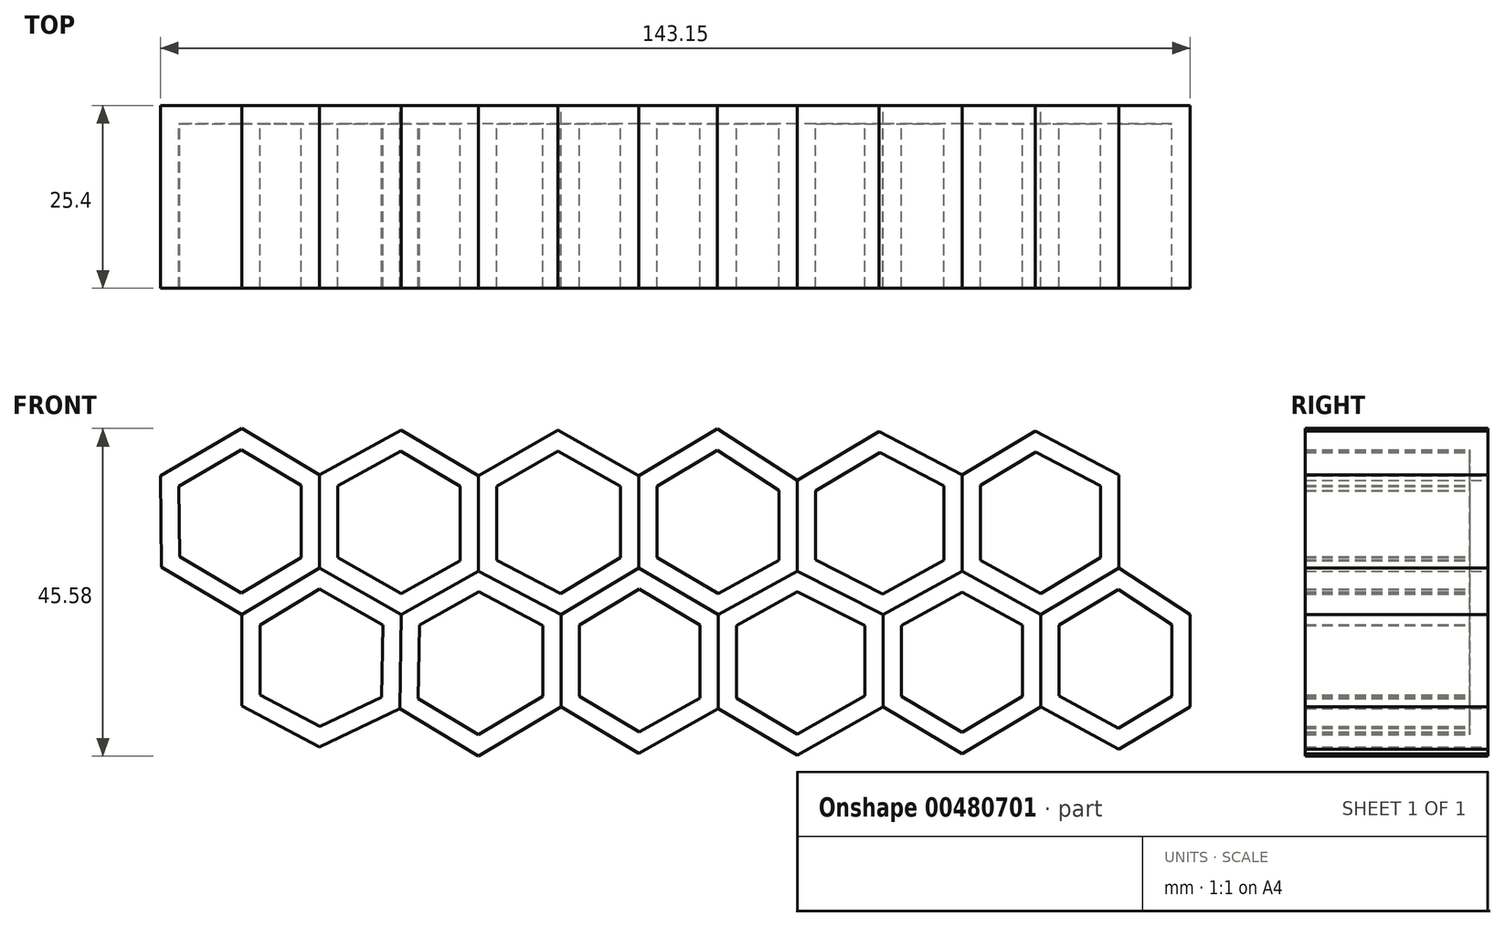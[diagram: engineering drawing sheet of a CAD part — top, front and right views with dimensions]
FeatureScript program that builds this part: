
annotation { "Feature Type Name" : "Feature", "Feature Type Description" : "" }
export const myFeature = defineFeature(function(context is Context, id is Id, definition is map)
    precondition{}
    {
        {
            var Q0;
            Q0=qCreatedBy(makeId("Front.planeOp"),FACE);
            var sketch = newSketch(context, id + "F0", { "sketchPlane" : qUnion([Q0])});
            skLineSegment(sketch, "E0", {"start": v(-72.86, 44.97) * mm, "end": v(-61.6, 51.55) * mm});
            skLineSegment(sketch, "E1", {"start": v(-61.6, 51.55) * mm, "end": v(-50.77, 45.08) * mm});
            skLineSegment(sketch, "E2", {"start": v(-50.77, 45.08) * mm, "end": v(-50.77, 32.14) * mm});
            skLineSegment(sketch, "E3", {"start": v(-50.77, 32.14) * mm, "end": v(-61.6, 25.66) * mm});
            skLineSegment(sketch, "E4", {"start": v(-61.6, 25.66) * mm, "end": v(-72.75, 32.25) * mm});
            skLineSegment(sketch, "E5", {"start": v(-72.75, 32.25) * mm, "end": v(-72.86, 44.97) * mm});
            skLineSegment(sketch, "E6", {"start": v(-50.77, 45.08) * mm, "end": v(-39.39, 51.33) * mm});
            skLineSegment(sketch, "E7", {"start": v(-39.39, 51.33) * mm, "end": v(-28.68, 44.97) * mm});
            skLineSegment(sketch, "E8", {"start": v(-28.68, 44.97) * mm, "end": v(-28.68, 31.69) * mm});
            skLineSegment(sketch, "E9", {"start": v(-28.68, 31.69) * mm, "end": v(-39.39, 25.66) * mm});
            skLineSegment(sketch, "E10", {"start": v(-39.39, 25.66) * mm, "end": v(-50.77, 32.14) * mm});
            skLineSegment(sketch, "E11", {"start": v(-28.68, 44.97) * mm, "end": v(-17.63, 51.33) * mm});
            skLineSegment(sketch, "E12", {"start": v(-17.63, 51.33) * mm, "end": v(-6.36, 44.97) * mm});
            skLineSegment(sketch, "E13", {"start": v(-6.36, 44.97) * mm, "end": v(-6.36, 32.14) * mm});
            skLineSegment(sketch, "E14", {"start": v(-6.36, 32.14) * mm, "end": v(-17.18, 25.66) * mm});
            skLineSegment(sketch, "E15", {"start": v(-17.18, 25.66) * mm, "end": v(-28.68, 31.69) * mm});
            skLineSegment(sketch, "E16", {"start": v(-6.36, 44.97) * mm, "end": v(4.57, 51.5) * mm});
            skLineSegment(sketch, "E17", {"start": v(4.57, 51.5) * mm, "end": v(15.63, 44.3) * mm});
            skLineSegment(sketch, "E18", {"start": v(15.63, 44.3) * mm, "end": v(15.63, 31.69) * mm});
            skLineSegment(sketch, "E19", {"start": v(15.63, 31.69) * mm, "end": v(4.65, 25.66) * mm});
            skLineSegment(sketch, "E20", {"start": v(4.65, 25.66) * mm, "end": v(-6.36, 32.14) * mm});
            skLineSegment(sketch, "E21", {"start": v(15.63, 44.3) * mm, "end": v(27.04, 51.13) * mm});
            skLineSegment(sketch, "E22", {"start": v(27.04, 51.13) * mm, "end": v(38.57, 45.08) * mm});
            skLineSegment(sketch, "E23", {"start": v(38.57, 45.08) * mm, "end": v(38.57, 31.69) * mm});
            skLineSegment(sketch, "E24", {"start": v(38.57, 31.69) * mm, "end": v(27.6, 25.66) * mm});
            skLineSegment(sketch, "E25", {"start": v(27.6, 25.66) * mm, "end": v(15.63, 31.69) * mm});
            skLineSegment(sketch, "E26", {"start": v(38.57, 45.08) * mm, "end": v(48.75, 51.16) * mm});
            skLineSegment(sketch, "E27", {"start": v(48.75, 51.16) * mm, "end": v(60.35, 45.08) * mm});
            skLineSegment(sketch, "E28", {"start": v(60.35, 45.08) * mm, "end": v(60.35, 32.14) * mm});
            skLineSegment(sketch, "E29", {"start": v(60.35, 32.14) * mm, "end": v(49.52, 25.66) * mm});
            skLineSegment(sketch, "E30", {"start": v(49.52, 25.66) * mm, "end": v(38.57, 31.69) * mm});
            skLineSegment(sketch, "E31", {"start": v(-61.6, 25.66) * mm, "end": v(-61.6, 12.94) * mm});
            skLineSegment(sketch, "E32", {"start": v(-61.6, 12.94) * mm, "end": v(-50.77, 7.26) * mm});
            skLineSegment(sketch, "E33", {"start": v(-50.77, 7.26) * mm, "end": v(-39.6, 12.56) * mm});
            skLineSegment(sketch, "E34", {"start": v(-39.6, 12.56) * mm, "end": v(-39.39, 25.66) * mm});
            skLineSegment(sketch, "E35", {"start": v(-17.18, 25.66) * mm, "end": v(-17.18, 12.84) * mm});
            skLineSegment(sketch, "E36", {"start": v(-17.18, 12.84) * mm, "end": v(-28.68, 5.97) * mm});
            skLineSegment(sketch, "E37", {"start": v(-28.68, 5.97) * mm, "end": v(-39.6, 12.56) * mm});
            skLineSegment(sketch, "E38", {"start": v(4.65, 25.66) * mm, "end": v(4.65, 12.56) * mm});
            skLineSegment(sketch, "E39", {"start": v(4.65, 12.56) * mm, "end": v(-6.36, 6.37) * mm});
            skLineSegment(sketch, "E40", {"start": v(-6.36, 6.37) * mm, "end": v(-17.18, 12.84) * mm});
            skLineSegment(sketch, "E41", {"start": v(27.6, 25.66) * mm, "end": v(27.6, 12.84) * mm});
            skLineSegment(sketch, "E42", {"start": v(27.6, 12.84) * mm, "end": v(15.63, 6.11) * mm});
            skLineSegment(sketch, "E43", {"start": v(15.63, 6.11) * mm, "end": v(4.65, 12.56) * mm});
            skLineSegment(sketch, "E44", {"start": v(49.52, 25.66) * mm, "end": v(49.52, 12.84) * mm});
            skLineSegment(sketch, "E45", {"start": v(49.52, 12.84) * mm, "end": v(38.57, 6.3) * mm});
            skLineSegment(sketch, "E46", {"start": v(38.57, 6.3) * mm, "end": v(27.6, 12.84) * mm});
            skLineSegment(sketch, "E47", {"start": v(60.35, 32.14) * mm, "end": v(70.29, 25.66) * mm});
            skLineSegment(sketch, "E48", {"start": v(70.29, 25.66) * mm, "end": v(70.29, 12.84) * mm});
            skLineSegment(sketch, "E49", {"start": v(70.29, 12.84) * mm, "end": v(60.35, 6.9) * mm});
            skLineSegment(sketch, "E50", {"start": v(60.35, 6.9) * mm, "end": v(49.52, 12.84) * mm});
            skSolve(sketch);
        }
        {
            var Q0;
            Q0=makeQuery(id+"F0.imprint","IMPRINT",FACE,{"disambiguationData":[TD([[makeQuery(id+"F0.imprint","IMPRINT",EDGE,{"derivedFrom":sQuery(id+"F0.wireOp",EDGE,"E0")}),-1.0]])]});
            var Q1;
            Q1=makeQuery(id+"F0.imprint","IMPRINT",FACE,{"disambiguationData":[TD([[makeQuery(id+"F0.imprint","IMPRINT",EDGE,{"derivedFrom":sQuery(id+"F0.wireOp",EDGE,"E29")}),1.0]])]});
            var Q2;
            Q2=makeQuery(id+"F0.imprint","IMPRINT",FACE,{"disambiguationData":[TD([[makeQuery(id+"F0.imprint","IMPRINT",EDGE,{"derivedFrom":sQuery(id+"F0.wireOp",EDGE,"E18")}),1.0]])]});
            var Q3;
            Q3=makeQuery(id+"F0.imprint","IMPRINT",FACE,{"disambiguationData":[TD([[makeQuery(id+"F0.imprint","IMPRINT",EDGE,{"derivedFrom":sQuery(id+"F0.wireOp",EDGE,"E14")}),1.0]])]});
            extrude(context, id + "F1", {"entities" : qUnion([Q0, Q1, Q2, Q3]), "depth" : 25.4 * mm});
        }
        {
            var Q0;
            Q0=makeQuery(id+"F1.opExtrude","CAP_FACE",FACE,{"disambiguationData":[OSD([sQuery(id+"F0.wireOp",EDGE,"E0"),sQuery(id+"F0.wireOp",EDGE,"E1"),sQuery(id+"F0.wireOp",EDGE,"E2"),sQuery(id+"F0.wireOp",EDGE,"E3"),sQuery(id+"F0.wireOp",EDGE,"E4"),sQuery(id+"F0.wireOp",EDGE,"E5")])],"isStart":false});
            var Q1;
            Q1=makeQuery(id+"F1.opExtrude","CAP_FACE",FACE,{"disambiguationData":[OSD([sQuery(id+"F0.wireOp",EDGE,"E14"),sQuery(id+"F0.wireOp",EDGE,"E20"),sQuery(id+"F0.wireOp",EDGE,"E35"),sQuery(id+"F0.wireOp",EDGE,"E38"),sQuery(id+"F0.wireOp",EDGE,"E39"),sQuery(id+"F0.wireOp",EDGE,"E40")])],"isStart":false});
            var Q2;
            Q2=makeQuery(id+"F1.opExtrude","CAP_FACE",FACE,{"disambiguationData":[OSD([sQuery(id+"F0.wireOp",EDGE,"E18"),sQuery(id+"F0.wireOp",EDGE,"E21"),sQuery(id+"F0.wireOp",EDGE,"E22"),sQuery(id+"F0.wireOp",EDGE,"E23"),sQuery(id+"F0.wireOp",EDGE,"E24"),sQuery(id+"F0.wireOp",EDGE,"E25")])],"isStart":false});
            var Q3;
            Q3=makeQuery(id+"F1.opExtrude","CAP_FACE",FACE,{"disambiguationData":[OSD([sQuery(id+"F0.wireOp",EDGE,"E29"),sQuery(id+"F0.wireOp",EDGE,"E44"),sQuery(id+"F0.wireOp",EDGE,"E47"),sQuery(id+"F0.wireOp",EDGE,"E48"),sQuery(id+"F0.wireOp",EDGE,"E49"),sQuery(id+"F0.wireOp",EDGE,"E50")])],"isStart":false});
            shell(context, id + "F2", {"entities" : qUnion([Q0, Q1, Q2, Q3]), "thickness" : 2.54 * mm});
        }
        {
            var Q0;
            Q0=makeQuery(id+"F0.imprint","IMPRINT",FACE,{"disambiguationData":[TD([[makeQuery(id+"F0.imprint","IMPRINT",EDGE,{"derivedFrom":sQuery(id+"F0.wireOp",EDGE,"E2")}),1.0]])]});
            var Q1;
            Q1=makeQuery(id+"F0.imprint","IMPRINT",FACE,{"disambiguationData":[TD([[makeQuery(id+"F0.imprint","IMPRINT",EDGE,{"derivedFrom":sQuery(id+"F0.wireOp",EDGE,"E13")}),1.0]])]});
            extrude(context, id + "F3", {"entities" : qUnion([Q0, Q1]), "depth" : 25.4 * mm});
        }
        {
            var Q0;
            Q0=makeQuery(id+"F3.opExtrude","CAP_FACE",FACE,{"disambiguationData":[OSD([sQuery(id+"F0.wireOp",EDGE,"E2"),sQuery(id+"F0.wireOp",EDGE,"E6"),sQuery(id+"F0.wireOp",EDGE,"E7"),sQuery(id+"F0.wireOp",EDGE,"E8"),sQuery(id+"F0.wireOp",EDGE,"E9"),sQuery(id+"F0.wireOp",EDGE,"E10")])],"isStart":false});
            var Q1;
            Q1=makeQuery(id+"F3.opExtrude","CAP_FACE",FACE,{"disambiguationData":[OSD([sQuery(id+"F0.wireOp",EDGE,"E13"),sQuery(id+"F0.wireOp",EDGE,"E16"),sQuery(id+"F0.wireOp",EDGE,"E17"),sQuery(id+"F0.wireOp",EDGE,"E18"),sQuery(id+"F0.wireOp",EDGE,"E19"),sQuery(id+"F0.wireOp",EDGE,"E20")])],"isStart":false});
            shell(context, id + "F4", {"entities" : qUnion([Q0, Q1]), "thickness" : 2.54 * mm});
        }
        {
            var Q0;
            Q0=makeQuery(id+"F0.imprint","IMPRINT",FACE,{"disambiguationData":[TD([[makeQuery(id+"F0.imprint","IMPRINT",EDGE,{"derivedFrom":sQuery(id+"F0.wireOp",EDGE,"E8")}),1.0]])]});
            var Q1;
            Q1=makeQuery(id+"F0.imprint","IMPRINT",FACE,{"disambiguationData":[TD([[makeQuery(id+"F0.imprint","IMPRINT",EDGE,{"derivedFrom":sQuery(id+"F0.wireOp",EDGE,"E3")}),1.0]])]});
            var Q2;
            Q2=makeQuery(id+"F0.imprint","IMPRINT",FACE,{"disambiguationData":[TD([[makeQuery(id+"F0.imprint","IMPRINT",EDGE,{"derivedFrom":sQuery(id+"F0.wireOp",EDGE,"E24")}),1.0]])]});
            extrude(context, id + "F5", {"entities" : qUnion([Q0, Q1, Q2]), "depth" : 25.4 * mm});
        }
        {
            var Q0;
            Q0=makeQuery(id+"F5.opExtrude","CAP_FACE",FACE,{"disambiguationData":[OSD([sQuery(id+"F0.wireOp",EDGE,"E3"),sQuery(id+"F0.wireOp",EDGE,"E10"),sQuery(id+"F0.wireOp",EDGE,"E31"),sQuery(id+"F0.wireOp",EDGE,"E32"),sQuery(id+"F0.wireOp",EDGE,"E33"),sQuery(id+"F0.wireOp",EDGE,"E34")])],"isStart":false});
            var Q1;
            Q1=makeQuery(id+"F5.opExtrude","CAP_FACE",FACE,{"disambiguationData":[OSD([sQuery(id+"F0.wireOp",EDGE,"E8"),sQuery(id+"F0.wireOp",EDGE,"E11"),sQuery(id+"F0.wireOp",EDGE,"E12"),sQuery(id+"F0.wireOp",EDGE,"E13"),sQuery(id+"F0.wireOp",EDGE,"E14"),sQuery(id+"F0.wireOp",EDGE,"E15")])],"isStart":false});
            var Q2;
            Q2=makeQuery(id+"F5.opExtrude","CAP_FACE",FACE,{"disambiguationData":[OSD([sQuery(id+"F0.wireOp",EDGE,"E24"),sQuery(id+"F0.wireOp",EDGE,"E30"),sQuery(id+"F0.wireOp",EDGE,"E41"),sQuery(id+"F0.wireOp",EDGE,"E44"),sQuery(id+"F0.wireOp",EDGE,"E45"),sQuery(id+"F0.wireOp",EDGE,"E46")])],"isStart":false});
            shell(context, id + "F6", {"entities" : qUnion([Q0, Q1, Q2]), "thickness" : 2.54 * mm});
        }
        {
            var Q0;
            Q0=makeQuery(id+"F0.imprint","IMPRINT",FACE,{"disambiguationData":[TD([[makeQuery(id+"F0.imprint","IMPRINT",EDGE,{"derivedFrom":sQuery(id+"F0.wireOp",EDGE,"E9")}),1.0]])]});
            var Q1;
            Q1=makeQuery(id+"F0.imprint","IMPRINT",FACE,{"disambiguationData":[TD([[makeQuery(id+"F0.imprint","IMPRINT",EDGE,{"derivedFrom":sQuery(id+"F0.wireOp",EDGE,"E19")}),1.0]])]});
            var Q2;
            Q2=makeQuery(id+"F0.imprint","IMPRINT",FACE,{"disambiguationData":[TD([[makeQuery(id+"F0.imprint","IMPRINT",EDGE,{"derivedFrom":sQuery(id+"F0.wireOp",EDGE,"E23")}),1.0]])]});
            extrude(context, id + "F7", {"entities" : qUnion([Q0, Q1, Q2]), "depth" : 25.4 * mm});
        }
        {
            var Q0;
            Q0=makeQuery(id+"F7.opExtrude","CAP_FACE",FACE,{"disambiguationData":[OSD([sQuery(id+"F0.wireOp",EDGE,"E9"),sQuery(id+"F0.wireOp",EDGE,"E15"),sQuery(id+"F0.wireOp",EDGE,"E34"),sQuery(id+"F0.wireOp",EDGE,"E35"),sQuery(id+"F0.wireOp",EDGE,"E36"),sQuery(id+"F0.wireOp",EDGE,"E37")])],"isStart":false});
            var Q1;
            Q1=makeQuery(id+"F7.opExtrude","CAP_FACE",FACE,{"disambiguationData":[OSD([sQuery(id+"F0.wireOp",EDGE,"E19"),sQuery(id+"F0.wireOp",EDGE,"E25"),sQuery(id+"F0.wireOp",EDGE,"E38"),sQuery(id+"F0.wireOp",EDGE,"E41"),sQuery(id+"F0.wireOp",EDGE,"E42"),sQuery(id+"F0.wireOp",EDGE,"E43")])],"isStart":false});
            var Q2;
            Q2=makeQuery(id+"F7.opExtrude","CAP_FACE",FACE,{"disambiguationData":[OSD([sQuery(id+"F0.wireOp",EDGE,"E23"),sQuery(id+"F0.wireOp",EDGE,"E26"),sQuery(id+"F0.wireOp",EDGE,"E27"),sQuery(id+"F0.wireOp",EDGE,"E28"),sQuery(id+"F0.wireOp",EDGE,"E29"),sQuery(id+"F0.wireOp",EDGE,"E30")])],"isStart":false});
            shell(context, id + "F8", {"entities" : qUnion([Q0, Q1, Q2]), "thickness" : 2.54 * mm});
        }
    });
